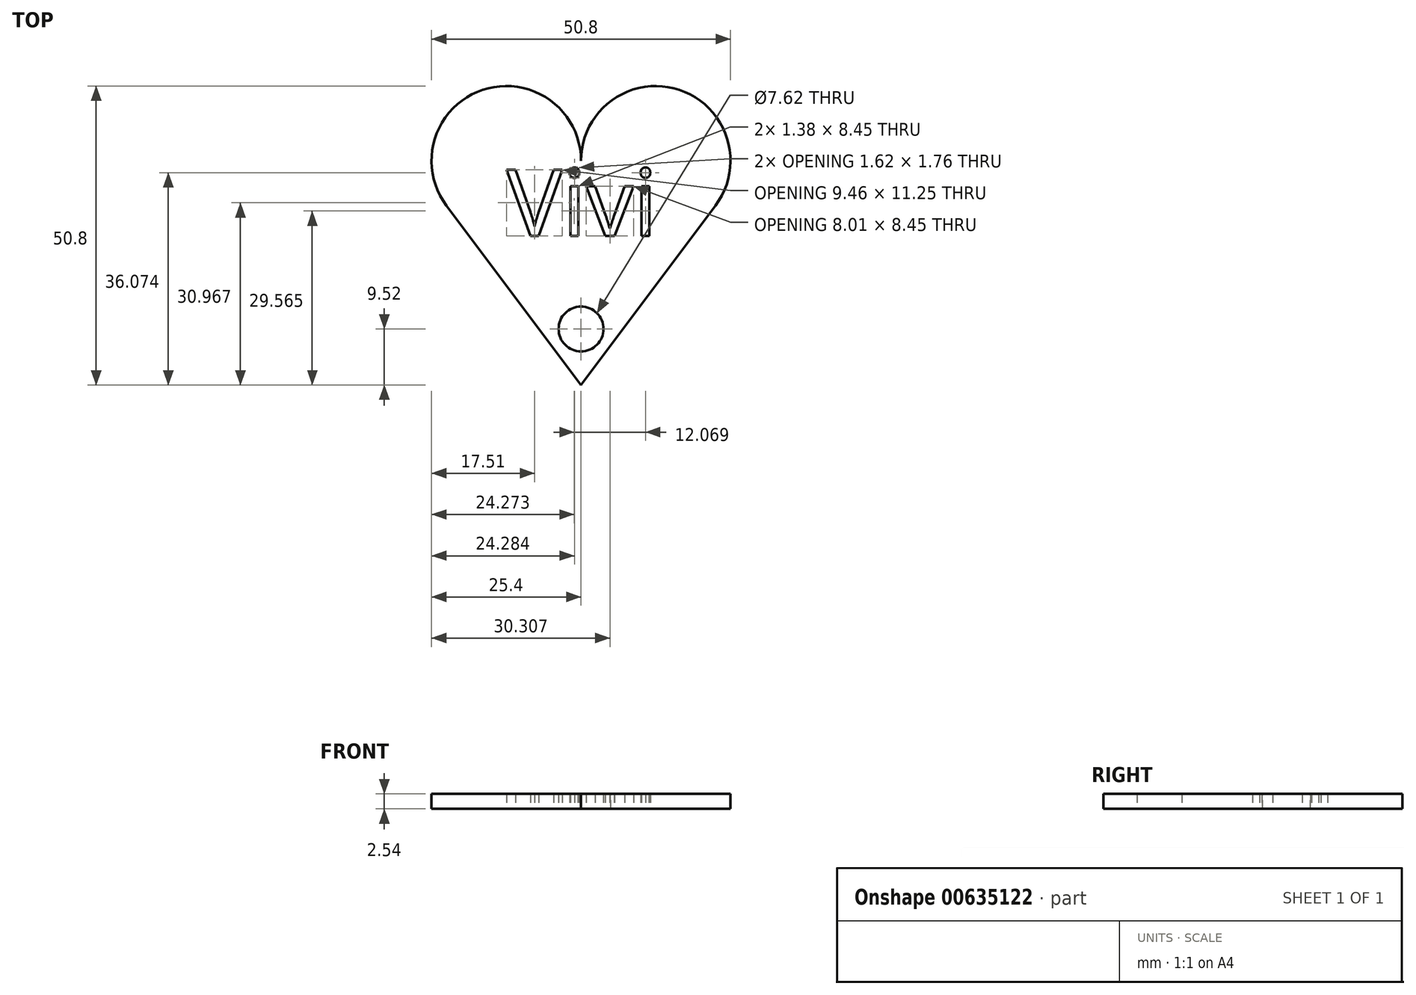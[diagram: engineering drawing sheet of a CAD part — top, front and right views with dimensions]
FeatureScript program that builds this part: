
annotation { "Feature Type Name" : "Feature", "Feature Type Description" : "" }
export const myFeature = defineFeature(function(context is Context, id is Id, definition is map)
    precondition{}
    {
        {
            var Q0;
            Q0=qCreatedBy(makeId("Top.planeOp"),FACE);
            var sketch = newSketch(context, id + "F0", { "sketchPlane" : qUnion([Q0])});
            skArc(sketch, "E0", {"start": v(0, 38.1) * mm, "mid": v(-16.72, 50.15) * mm, "end": v(-22.86, 30.48) * mm});
            skArc(sketch, "E1", {"start": v(22.86, 30.48) * mm, "mid": v(16.72, 50.15) * mm, "end": v(0, 38.1) * mm});
            skLineSegment(sketch, "E2", {"start": v(0, 0) * mm, "end": v(-22.86, 30.48) * mm});
            skLineSegment(sketch, "E3", {"start": v(0, 0) * mm, "end": v(22.86, 30.48) * mm});
            skText(sketch, "E4", { "text": "Vivi", "fontName": "NotoSans-Regular.ttf"});
            skPoint(sketch, "E5.center.orphan", {"position": v(0, 7.08) * mm});
            skCircle(sketch, "E6", {"center": v(0, 9.52) * mm, "radius": 3.81 * mm});
            const initialGuessF0  = {"E4": [-0.01262, 0.02534, 1, 0, 0.01135]};
            skSetInitialGuess(sketch, initialGuessF0);
            skSolve(sketch);
        }
        {
            var Q0;
            Q0=makeQuery(id+"F0.imprint","IMPRINT",FACE,{"disambiguationData":[TD([[makeQuery(id+"F0.imprint","IMPRINT",EDGE,{"derivedFrom":sQuery(id+"F0.wireOp",EDGE,"E0")}),1.0]])]});
            extrude(context, id + "F1", {"entities" : qUnion([Q0]), "depth" : 2.54 * mm, "offsetDistance" : 25.4 * mm});
        }
    });
